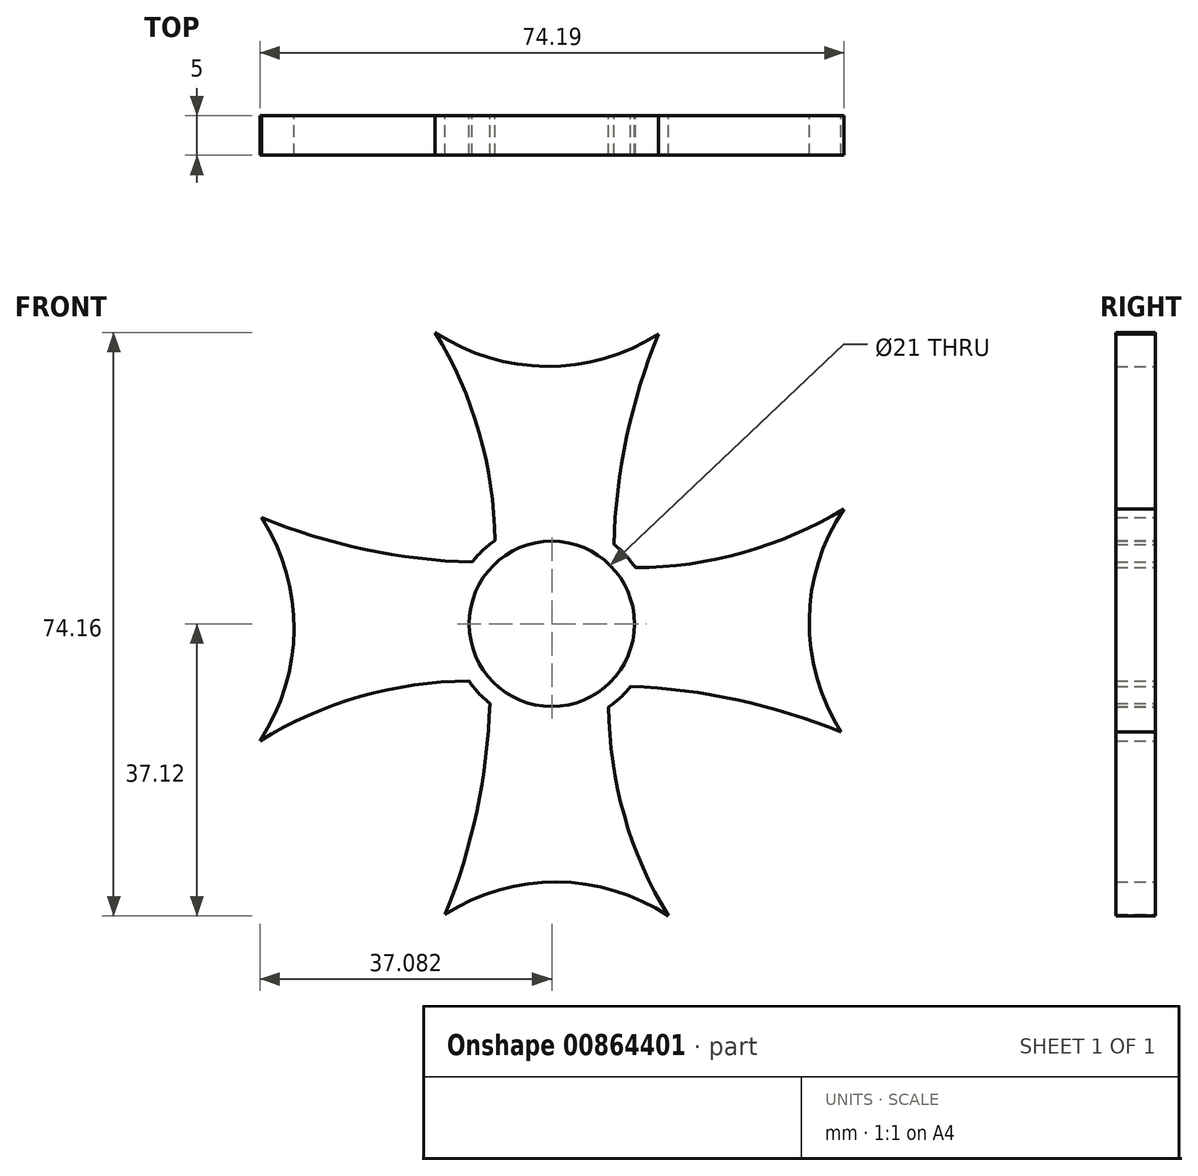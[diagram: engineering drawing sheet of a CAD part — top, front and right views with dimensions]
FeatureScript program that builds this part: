
annotation { "Feature Type Name" : "Feature", "Feature Type Description" : "" }
export const myFeature = defineFeature(function(context is Context, id is Id, definition is map)
    precondition{}
    {
        {
            var Q0;
            Q0=qCreatedBy(makeId("Front.planeOp"),FACE);
            var sketch = newSketch(context, id + "F0", { "sketchPlane" : qUnion([Q0])});
            skPoint(sketch, "E0.center.orphan", {"position": v(0, 0) * mm});
            skArc(sketch, "E1", {"start": v(14.8, -37.04) * mm, "mid": v(0.67, -32.7) * mm, "end": v(-13.53, -36.82) * mm});
            skArc(sketch, "E2", {"start": v(-13.53, -36.82) * mm, "mid": v(-9.5, -23.67) * mm, "end": v(-7.87, -10) * mm});
            skPoint(sketch, "E3.center.orphan", {"position": v(0, 0.04) * mm});
            skArc(sketch, "E4", {"start": v(37.1, 14.67) * mm, "mid": v(32.7, 0.55) * mm, "end": v(36.76, -13.67) * mm});
            skArc(sketch, "E5", {"start": v(36.76, -13.67) * mm, "mid": v(23.65, -9.59) * mm, "end": v(10.02, -7.88) * mm});
            skPoint(sketch, "E6.center.orphan", {"position": v(-0.04, 0.04) * mm});
            skArc(sketch, "E7", {"start": v(-37.08, -14.77) * mm, "mid": v(-32.74, -0.63) * mm, "end": v(-36.86, 13.57) * mm});
            skArc(sketch, "E8", {"start": v(-36.86, 13.57) * mm, "mid": v(-23.74, 9.55) * mm, "end": v(-10.12, 7.92) * mm});
            skPoint(sketch, "E9.center.orphan", {"position": v(0, 0.08) * mm});
            skArc(sketch, "E10", {"start": v(-14.8, 37.12) * mm, "mid": v(-0.67, 32.79) * mm, "end": v(13.53, 36.9) * mm});
            skArc(sketch, "E11", {"start": v(13.53, 36.9) * mm, "mid": v(9.52, 23.79) * mm, "end": v(7.88, 10.17) * mm});
            skArc(sketch, "E12.trimOffspring", {"start": v(-7.22, 10.64) * mm, "mid": v(-9.22, 24.4) * mm, "end": v(-14.8, 37.12) * mm});
            skArc(sketch, "E13.trimOffspring", {"start": v(10.63, 7.21) * mm, "mid": v(24.37, 9.15) * mm, "end": v(37.1, 14.67) * mm});
            skArc(sketch, "E14.trimOffspring", {"start": v(7.22, -10.48) * mm, "mid": v(9.2, -24.28) * mm, "end": v(14.8, -37.04) * mm});
            skArc(sketch, "E15.trimOffspring", {"start": v(-10.53, -7.18) * mm, "mid": v(-24.32, -9.17) * mm, "end": v(-37.08, -14.77) * mm});
            skCircle(sketch, "E16", {"center": v(0, 0.08) * mm, "radius": 10.5 * mm});
            skArc(sketch, "E17", {"start": v(10.63, 7.21) * mm, "mid": v(9.37, 8.8) * mm, "end": v(7.88, 10.17) * mm});
            skArc(sketch, "E18.trimOffspring", {"start": v(-7.22, 10.64) * mm, "mid": v(-8.78, 9.4) * mm, "end": v(-10.12, 7.92) * mm});
            skArc(sketch, "E19.trimOffspring", {"start": v(-10.53, -7.18) * mm, "mid": v(-9.31, -8.7) * mm, "end": v(-7.87, -10) * mm});
            skArc(sketch, "E20.trimOffspring", {"start": v(7.22, -10.48) * mm, "mid": v(8.72, -9.29) * mm, "end": v(10.02, -7.88) * mm});
            skSolve(sketch);
        }
        {
            var Q0;
            Q0=makeQuery(id+"F0.imprint","IMPRINT",FACE,{"disambiguationData":[TD([[makeQuery(id+"F0.imprint","IMPRINT",EDGE,{"derivedFrom":sQuery(id+"F0.wireOp",EDGE,"E1")}),-1.0]])]});
            extrude(context, id + "F1", {"entities" : qUnion([Q0]), "depth" : 5 * mm, "offsetDistance" : 25.4 * mm});
        }
    });
